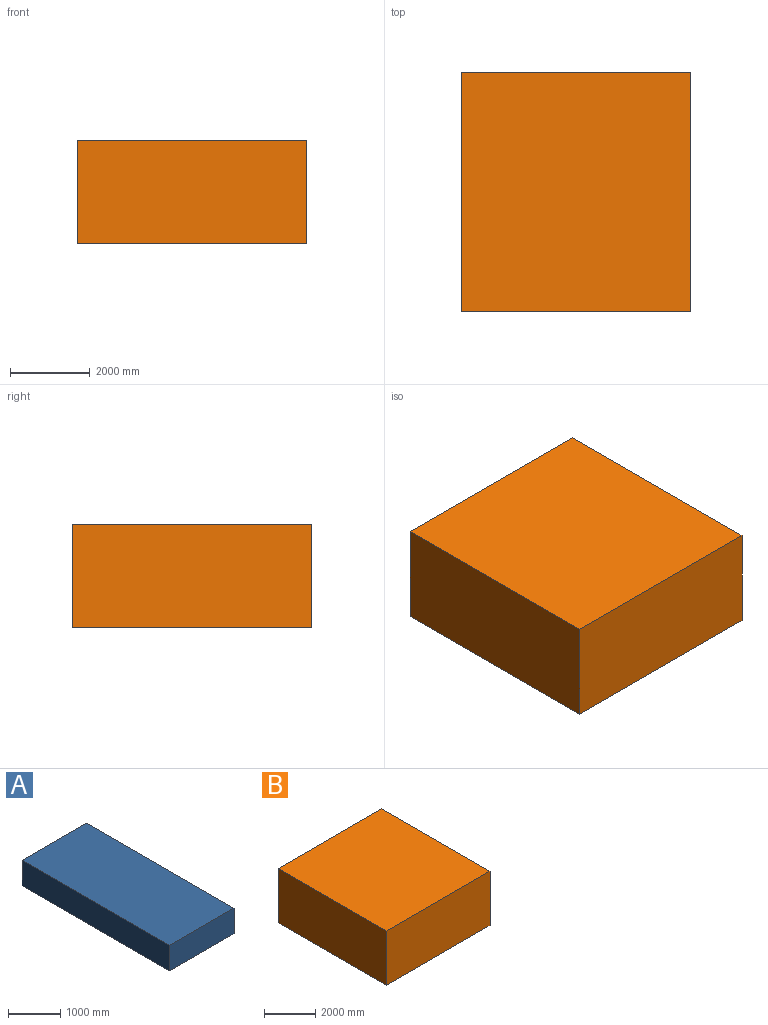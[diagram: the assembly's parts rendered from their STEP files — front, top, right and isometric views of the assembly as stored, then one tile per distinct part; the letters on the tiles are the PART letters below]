
ASSEMBLY  parts=2 mates=1
PART A: 6 faces, bbox 1750x4000x600 mm
  f0: plane 4000x1750mm, normal (0,0,1), area 7000000mm2, adj f1,f3,f4,f5
  f1: plane 4000x600mm, normal (-1,0,0), area 2400000mm2, adj f0,f2,f4,f5
  f2: plane 4000x1750mm, normal (0,0,-1), area 7000000mm2, adj f1,f3,f4,f5
  f3: plane 4000x600mm, normal (1,0,0), area 2400000mm2, adj f0,f2,f4,f5
  f4: plane 1750x600mm, normal (0,-1,0), area 1050000mm2, adj f0,f1,f2,f3
  f5: plane 1750x600mm, normal (0,1,0), area 1050000mm2, adj f0,f1,f2,f3
PART B: 11 faces, bbox 5750x6000x2600 mm
  f0: plane 4000x1750mm, normal (0,0,-1), area 7000000mm2, adj f1,f2,f9,f10
  f1: plane 4000x600mm, normal (1,0,0), area 2400000mm2, adj f0,f8,f9,f10
  f2: plane 4000x600mm, normal (-1,0,0), area 2400000mm2, adj f0,f8,f9,f10
  f3: plane 6000x2600mm, normal (-1,0,0), area 15600000mm2, adj f5,f6,f7,f8
  f4: plane 6000x2600mm, normal (1,0,0), area 15600000mm2, adj f5,f6,f7,f8
  f5: plane 5750x2600mm, normal (0,-1,0), area 14950000mm2, adj f3,f4,f7,f8
  f6: plane 5750x2600mm, normal (0,1,0), area 14950000mm2, adj f3,f4,f7,f8
  f7: plane 6000x5750mm, normal (0,0,1), area 34500000mm2, adj f3,f4,f5,f6
  f8: plane 6000x5750mm, normal (0,0,-1), area 27500000mm2, adj f1,f2,f3,f4,f5,f6,f9,f10
  f9: plane 1750x600mm, normal (0,1,0), area 1050000mm2, adj f0,f1,f2,f8
  f10: plane 1750x600mm, normal (0,-1,0), area 1050000mm2, adj f0,f1,f2,f8
PLACE A t=(-874.45,1995.08,-310.36)mm
PLACE B t=(-2874.45,2995.08,-310.36)mm fixed
MATE fastened A.f2 <-> B.f8  axis (0,0,-1) through (0.55,-4.92,-310.36)mm
